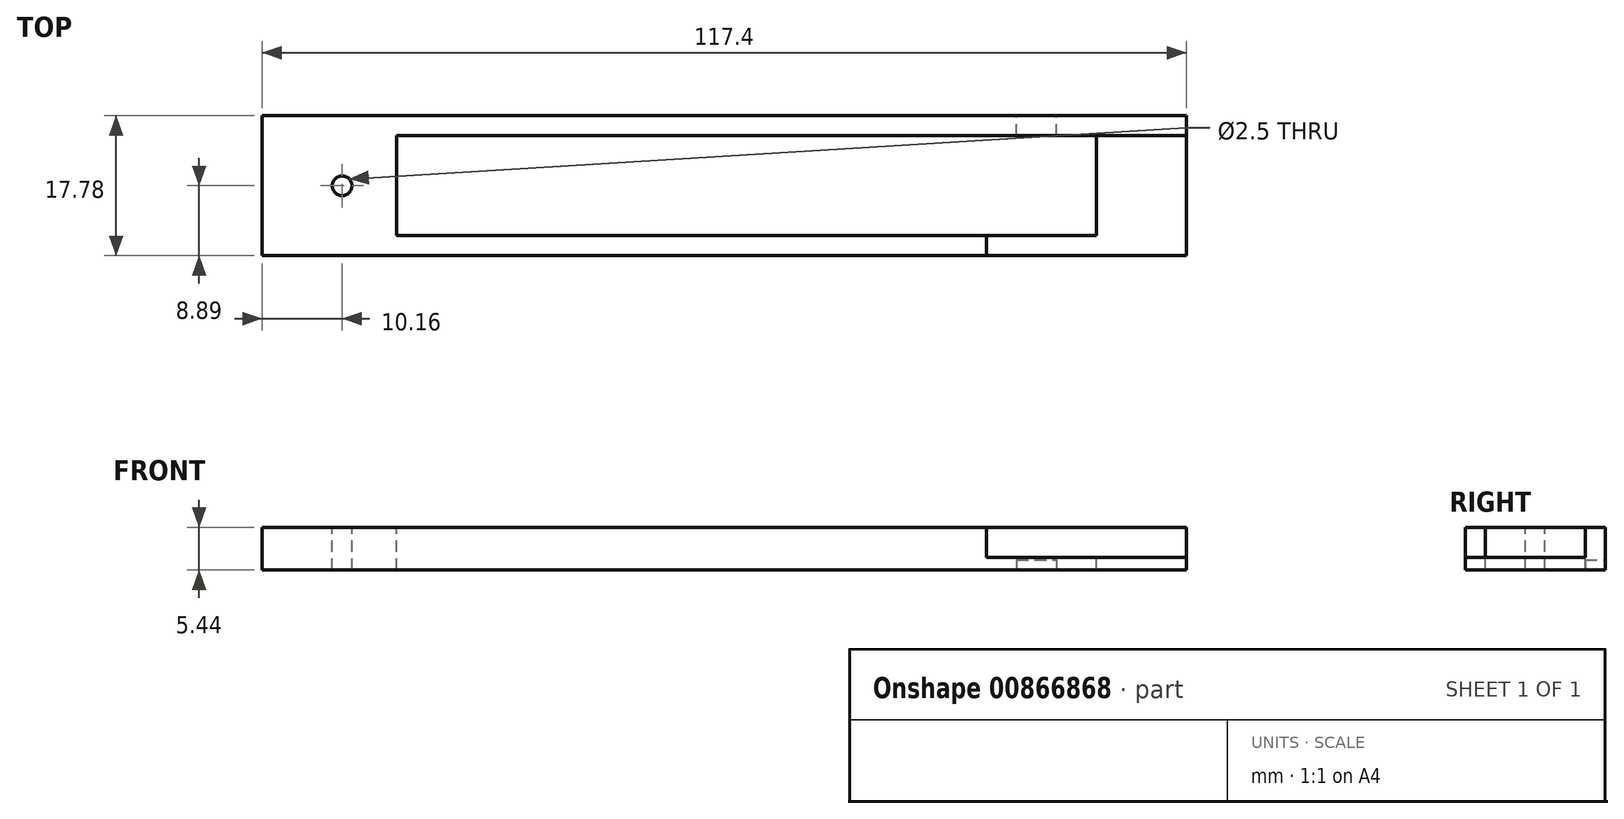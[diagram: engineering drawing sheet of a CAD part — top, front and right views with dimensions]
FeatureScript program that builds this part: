
annotation { "Feature Type Name" : "Feature", "Feature Type Description" : "" }
export const myFeature = defineFeature(function(context is Context, id is Id, definition is map)
    precondition{}
    {
        {
            var Q0;
            Q0=qCreatedBy(makeId("Top.planeOp"),FACE);
            var sketch = newSketch(context, id + "F0", { "sketchPlane" : qUnion([Q0])});
            skLineSegment(sketch, "E0.bottom", {"start": v(0, 0) * mm, "end": v(117.4, 0) * mm});
            skLineSegment(sketch, "E0.top", {"start": v(0, 17.78) * mm, "end": v(117.4, 17.78) * mm});
            skLineSegment(sketch, "E0.left", {"start": v(0, 0) * mm, "end": v(0, 17.78) * mm});
            skLineSegment(sketch, "E0.right", {"start": v(117.4, 0) * mm, "end": v(117.4, 17.78) * mm});
            skSolve(sketch);
        }
        {
            var Q0;
            Q0=makeQuery(id+"F0.imprint","IMPRINT",FACE,{"disambiguationData":[TD([[makeQuery(id+"F0.imprint","IMPRINT",EDGE,{"derivedFrom":sQuery(id+"F0.wireOp",EDGE,"E0.bottom")}),1.0]])]});
            extrude(context, id + "F1", {"entities" : qUnion([Q0]), "depth" : 5.44 * mm, "offsetDistance" : 25.4 * mm});
        }
        {
            var Q0;
            Q0=makeQuery(id+"F1.opExtrude","CAP_FACE",FACE,{"disambiguationData":[OSD([sQuery(id+"F0.wireOp",EDGE,"E0.bottom"),sQuery(id+"F0.wireOp",EDGE,"E0.top"),sQuery(id+"F0.wireOp",EDGE,"E0.left"),sQuery(id+"F0.wireOp",EDGE,"E0.right")])],"isStart":false});
            var sketch = newSketch(context, id + "F2", { "sketchPlane" : qUnion([Q0])});
            skLineSegment(sketch, "E1.bottom", {"start": v(17.07, 15.24) * mm, "end": v(105.97, 15.24) * mm});
            skLineSegment(sketch, "E1.top", {"start": v(17.07, 2.54) * mm, "end": v(105.97, 2.54) * mm});
            skLineSegment(sketch, "E1.left", {"start": v(17.07, 15.24) * mm, "end": v(17.07, 2.54) * mm});
            skLineSegment(sketch, "E1.right", {"start": v(105.97, 15.24) * mm, "end": v(105.97, 2.54) * mm});
            skSolve(sketch);
        }
        {
            var Q0;
            Q0=makeQuery(id+"F2.imprint","IMPRINT",FACE,{"disambiguationData":[TD([[makeQuery(id+"F2.imprint","IMPRINT",EDGE,{"derivedFrom":sQuery(id+"F2.wireOp",EDGE,"E1.bottom")}),-1.0]])]});
            extrude(context, id + "F3", {"entities" : qUnion([Q0]), "operationType" : NewBodyOperationType.REMOVE, "oppositeDirection" : true, "depth" : 25.4 * mm, "offsetDistance" : 25.4 * mm});
        }
        {
            var Q0;
            Q0=makeQuery(id+"F1.opExtrude","CAP_FACE",FACE,{"disambiguationData":[OSD([sQuery(id+"F0.wireOp",EDGE,"E0.bottom"),sQuery(id+"F0.wireOp",EDGE,"E0.top"),sQuery(id+"F0.wireOp",EDGE,"E0.left"),sQuery(id+"F0.wireOp",EDGE,"E0.right")])],"isStart":false});
            var sketch = newSketch(context, id + "F4", { "sketchPlane" : qUnion([Q0])});
            skLineSegment(sketch, "E2.bottom", {"start": v(105.97, 15.24) * mm, "end": v(117.4, 15.24) * mm});
            skLineSegment(sketch, "E2.top", {"start": v(105.97, 2.54) * mm, "end": v(117.4, 2.54) * mm});
            skLineSegment(sketch, "E2.left", {"start": v(105.97, 15.24) * mm, "end": v(105.97, 2.54) * mm});
            skLineSegment(sketch, "E2.right", {"start": v(117.4, 15.24) * mm, "end": v(117.4, 2.54) * mm});
            skSolve(sketch);
        }
        {
            var Q0;
            Q0=makeQuery(id+"F4.imprint","IMPRINT",FACE,{"disambiguationData":[TD([[makeQuery(id+"F4.imprint","IMPRINT",EDGE,{"derivedFrom":sQuery(id+"F4.wireOp",EDGE,"E2.bottom")}),-1.0]])]});
            extrude(context, id + "F5", {"entities" : qUnion([Q0]), "operationType" : NewBodyOperationType.REMOVE, "oppositeDirection" : true, "depth" : 3.8 * mm, "offsetDistance" : 25.4 * mm});
        }
        {
            var Q0;
            Q0=makeQuery(id+"F5.boolean.opBoolean","COPY",FACE,{"derivedFrom":makeQuery(id+"F5.opExtrude","CAP_FACE",FACE,{"disambiguationData":[OSD([sQuery(id+"F4.wireOp",EDGE,"E2.bottom"),sQuery(id+"F4.wireOp",EDGE,"E2.top"),sQuery(id+"F4.wireOp",EDGE,"E2.left"),sQuery(id+"F4.wireOp",EDGE,"E2.right")])],"isStart":false})});
            var sketch = newSketch(context, id + "F6", { "sketchPlane" : qUnion([Q0])});
            skLineSegment(sketch, "E3.bottom", {"start": v(117.4, 15.24) * mm, "end": v(92, 15.24) * mm});
            skLineSegment(sketch, "E3.top", {"start": v(117.4, 0) * mm, "end": v(92, 0) * mm});
            skLineSegment(sketch, "E3.left", {"start": v(117.4, 15.24) * mm, "end": v(117.4, 0) * mm});
            skLineSegment(sketch, "E3.right", {"start": v(92, 15.24) * mm, "end": v(92, 0) * mm});
            skSolve(sketch);
        }
        {
            var Q0;
            {var subQ3=sQuery(id+"F6.wireOp",EDGE,"E3.top");Q0=makeQuery(id+"F6.imprint","IMPRINT",FACE,{"disambiguationData":[TD([[makeQuery(id+"F6.imprint","IMPRINT",EDGE,{"derivedFrom":subQ3}),-1.0]])]});}
            extrude(context, id + "F7", {"entities" : qUnion([Q0]), "operationType" : NewBodyOperationType.REMOVE, "endBound" : BoundingType.UP_TO_NEXT, "depth" : 5.08 * mm, "offsetDistance" : 25.4 * mm});
        }
        {
            var Q0;
            Q0=makeQuery(id+"F1.opExtrude","CAP_FACE",FACE,{"disambiguationData":[OSD([sQuery(id+"F0.wireOp",EDGE,"E0.bottom"),sQuery(id+"F0.wireOp",EDGE,"E0.top"),sQuery(id+"F0.wireOp",EDGE,"E0.left"),sQuery(id+"F0.wireOp",EDGE,"E0.right")])],"isStart":false});
            var sketch = newSketch(context, id + "F8", { "sketchPlane" : qUnion([Q0])});
            skCircle(sketch, "E4", {"center": v(10.16, 8.9) * mm, "radius": 1.25 * mm});
            skPoint(sketch, "E4.centerSnap0", {"position": v(0, 8.9) * mm});
            skSolve(sketch);
        }
        {
            var Q0;
            Q0=makeQuery(id+"F8.imprint","IMPRINT",FACE,{"disambiguationData":[TD([[makeQuery(id+"F8.imprint","IMPRINT",EDGE,{"derivedFrom":sQuery(id+"F8.wireOp",EDGE,"E4")}),1.0]])]});
            extrude(context, id + "F9", {"entities" : qUnion([Q0]), "operationType" : NewBodyOperationType.REMOVE, "endBound" : BoundingType.UP_TO_NEXT, "oppositeDirection" : true, "depth" : 25.4 * mm, "offsetDistance" : 25.4 * mm});
        }
        {
            var Q0;
            Q0=makeQuery(id+"F1.opExtrude","CAP_FACE",FACE,{"disambiguationData":[OSD([sQuery(id+"F0.wireOp",EDGE,"E0.bottom"),sQuery(id+"F0.wireOp",EDGE,"E0.top"),sQuery(id+"F0.wireOp",EDGE,"E0.left"),sQuery(id+"F0.wireOp",EDGE,"E0.right")])],"isStart":true});
            var sketch = newSketch(context, id + "F10", { "sketchPlane" : qUnion([Q0])});
            skLineSegment(sketch, "E5.bottom", {"start": v(100.89, -15.24) * mm, "end": v(95.8, -15.24) * mm});
            skLineSegment(sketch, "E5.top", {"start": v(100.89, -17.78) * mm, "end": v(95.8, -17.78) * mm});
            skLineSegment(sketch, "E5.left", {"start": v(100.89, -15.24) * mm, "end": v(100.89, -17.78) * mm});
            skLineSegment(sketch, "E5.right", {"start": v(95.8, -15.24) * mm, "end": v(95.8, -17.78) * mm});
            skSolve(sketch);
        }
        {
            var Q0;
            Q0=makeQuery(id+"F10.imprint","IMPRINT",FACE,{"disambiguationData":[TD([[makeQuery(id+"F10.imprint","IMPRINT",EDGE,{"derivedFrom":sQuery(id+"F10.wireOp",EDGE,"E5.bottom")}),-1.0]])]});
            extrude(context, id + "F11", {"entities" : qUnion([Q0]), "operationType" : NewBodyOperationType.REMOVE, "oppositeDirection" : true, "depth" : 1.27 * mm, "offsetDistance" : 25.4 * mm});
        }
    });
